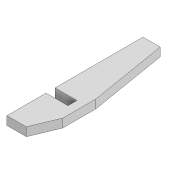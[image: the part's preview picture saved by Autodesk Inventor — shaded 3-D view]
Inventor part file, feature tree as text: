
AUTODESK INVENTOR PART (.ipt)
format: ipt  version: 2022 (Build 260153000, 153)  size: 94,720 bytes
history: native  units: mm
features: chamfer x2, extrude x1, sketch x1
ambient origin geometry x8: Origin, YZ Plane, XZ Plane, XY Plane, X Axis, Y Axis, Z Axis, Center Point
bodies: Solid1 (feature_tree)
feature tree (4):
  extrude  "Extrusion1"  Depth=31.7mm
  chamfer  "Chamfer1"  Distance=2.1mm
  chamfer  "Chamfer2"  Distance=5.1mm
  sketch  "Sketch1"  dims[d0=7.0mm d1=31.7mm d2=2.1mm d3=5.1mm d4=9.1mm d5=2.0mm d6=0.0mm d7=2.5mm d8=6.0mm d9=45.0deg d10=18.0mm d11=3.0mm d12=45.0deg]
